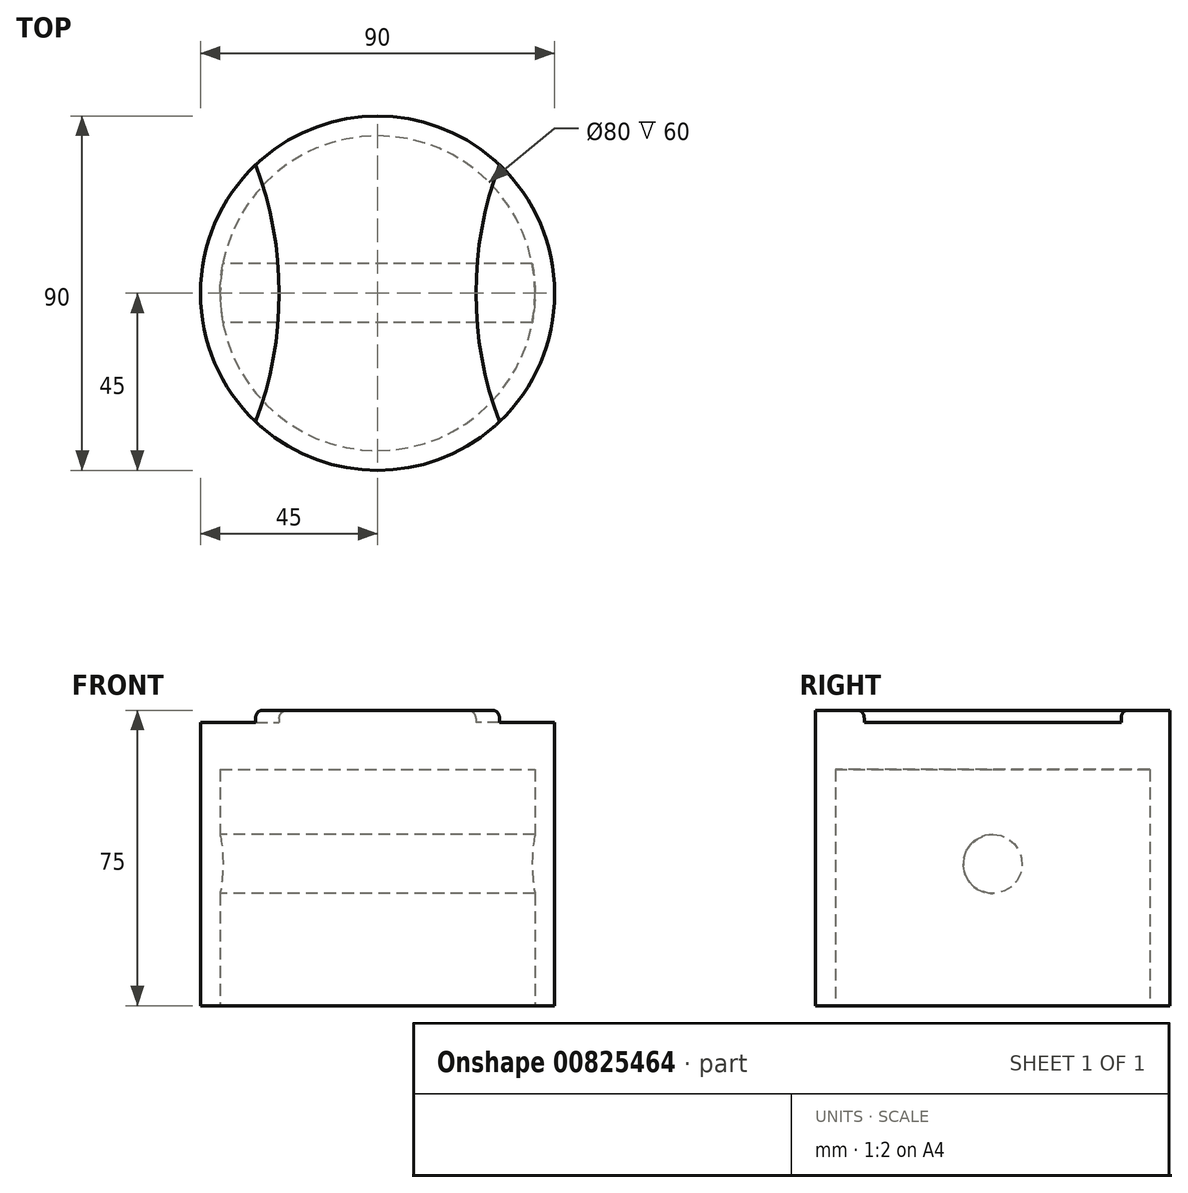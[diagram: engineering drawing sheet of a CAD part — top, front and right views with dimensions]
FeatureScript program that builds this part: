
annotation { "Feature Type Name" : "Feature", "Feature Type Description" : "" }
export const myFeature = defineFeature(function(context is Context, id is Id, definition is map)
    precondition{}
    {
        {
            var Q0;
            Q0=qCreatedBy(makeId("Top.planeOp"),FACE);
            var sketch = newSketch(context, id + "F0", { "sketchPlane" : qUnion([Q0])});
            skCircle(sketch, "E0", {"center": v(0, 0) * mm, "radius": 45 * mm});
            skSolve(sketch);
        }
        {
            var Q0;
            Q0 = qSketchRegion(id + "F0", true);
            extrude(context, id + "F1", {"entities" : qUnion([Q0]), "depth" : 72 * mm, "offsetDistance" : 25 * mm});
        }
        {
            var Q0;
            Q0=makeQuery(id+"F1.opExtrude","CAP_FACE",FACE,{"disambiguationData":[OSD([sQuery(id+"F0.wireOp",EDGE,"E0")])],"isStart":true});
            var sketch = newSketch(context, id + "F2", { "sketchPlane" : qUnion([Q0])});
            skCircle(sketch, "E1", {"center": v(0, 0) * mm, "radius": 40 * mm});
            skSolve(sketch);
        }
        {
            var Q0;
            Q0 = qSketchRegion(id + "F2", true);
            extrude(context, id + "F3", {"entities" : qUnion([Q0]), "operationType" : NewBodyOperationType.REMOVE, "oppositeDirection" : true, "depth" : 60 * mm, "offsetDistance" : 25 * mm});
        }
        {
            var Q0;
            Q0=makeQuery(id+"F1.opExtrude","CAP_FACE",FACE,{"disambiguationData":[OSD([sQuery(id+"F0.wireOp",EDGE,"E0")])],"isStart":false});
            var sketch = newSketch(context, id + "F4", { "sketchPlane" : qUnion([Q0])});
            skArc(sketch, "E2", {"start": v(30.98, 32.64) * mm, "mid": v(25, 0) * mm, "end": v(30.98, -32.64) * mm});
            skArc(sketch, "E3.MirrorCS", {"start": v(-30.98, 32.64) * mm, "mid": v(-25, 0) * mm, "end": v(-30.98, -32.64) * mm});
            skSolve(sketch);
        }
        {
            var Q0;
            {var subQ0=sQuery(id+"F4.wireOp",EDGE,"E2");Q0=makeQuery(id+"F4.imprint","IMPRINT",FACE,{"disambiguationData":[TD([[makeQuery(id+"F4.imprint","IMPRINT",EDGE,{"derivedFrom":subQ0}),-1.0]])]});}
            extrude(context, id + "F5", {"entities" : qUnion([Q0]), "operationType" : NewBodyOperationType.ADD, "depth" : 3 * mm, "offsetDistance" : 25 * mm});
        }
        {
            var Q0;
            Q0=makeQuery(id+"F5.opExtrude","CAP_EDGE",EDGE,{"disambiguationData":[OSD([sQuery(id+"F4.wireOp",EDGE,"E2")])],"isStart":false});
            var Q1;
            Q1=makeQuery(id+"F5.opExtrude","CAP_EDGE",EDGE,{"disambiguationData":[OSD([sQuery(id+"F4.wireOp",EDGE,"E3.MirrorCS")])],"isStart":false});
            fillet(context, id + "F6", {"entities" : qUnion([Q0, Q1]), "radius" : 2 * mm, "tangentPropagation" : true, "allowEdgeOverflow" : false});
        }
        {
            var Q0;
            Q0=qCreatedBy(makeId("Right.planeOp"),FACE);
            var sketch = newSketch(context, id + "F7", { "sketchPlane" : qUnion([Q0])});
            skPoint(sketch, "E4", {"position": v(0, 36) * mm});
            skCircle(sketch, "E5", {"center": v(0, 36) * mm, "radius": 7.5 * mm});
            skSolve(sketch);
        }
        {
            var Q0;
            Q0=makeQuery(id+"F7.imprint","IMPRINT",FACE,{"disambiguationData":[TD([[makeQuery(id+"F7.imprint","IMPRINT",EDGE,{"derivedFrom":sQuery(id+"F7.wireOp",EDGE,"E5")}),1.0]])]});
            var Q1;
            Q1=sQuery(id+"F7.wireOp",EDGE,"E5");
            extrude(context, id + "F8", {"entities" : qUnion([Q0]), "operationType" : NewBodyOperationType.ADD, "surfaceEntities" : qUnion([Q1]), "depth" : 40 * mm, "offsetDistance" : 25 * mm, "hasSecondDirection" : true, "secondDirectionOppositeDirection" : true, "secondDirectionDepth" : 40 * mm});
        }
        {
            var Q0;
            Q0=makeQuery(id+"F7.imprint","IMPRINT",FACE,{"disambiguationData":[TD([[makeQuery(id+"F7.imprint","IMPRINT",EDGE,{"derivedFrom":sQuery(id+"F7.wireOp",EDGE,"E5")}),1.0]])]});
            var Q1;
            Q1=sQuery(id+"F7.wireOp",EDGE,"E5");
            extrude(context, id + "F9", {"entities" : qUnion([Q0]), "operationType" : NewBodyOperationType.ADD, "surfaceOperationType" : NewSurfaceOperationType.ADD, "surfaceEntities" : qUnion([Q1]), "oppositeDirection" : true, "depth" : 35 * mm, "offsetDistance" : 25 * mm, "hasSecondDirection" : true, "secondDirectionOppositeDirection" : true, "secondDirectionDepth" : 25 * mm});
        }
    });
